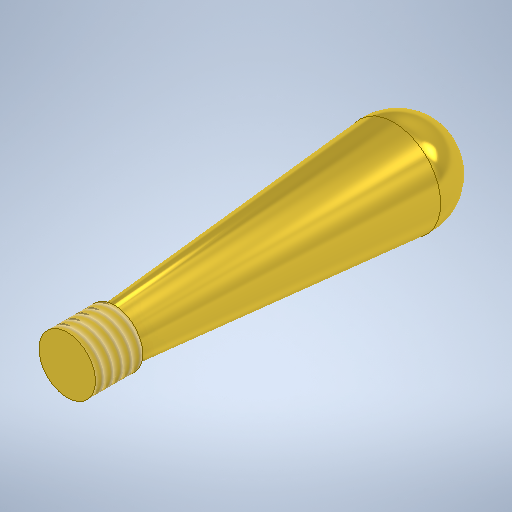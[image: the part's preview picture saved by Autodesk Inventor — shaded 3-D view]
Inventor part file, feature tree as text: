
AUTODESK INVENTOR PART (.ipt)
format: ipt  version: 2025.1 (Build 291241000, 241)  size: 293,888 bytes
history: native  units: mm
features: revolve x1, thread x1, sketch x1
ambient origin geometry x8: Origin, YZ Plane, XZ Plane, XY Plane, X Axis, Y Axis, Z Axis, Center Point
bodies: Solid1 (feature_tree)
feature tree (3):
  revolve  "Revolution1"  [1 undecoded]
  thread  "Thread1"  [1 undecoded]
  sketch  "Sketch1"  dims[d0=3.0mm d3=2.5mm d4=90.0deg d5=20.0mm d6=2.5mm d9=2.5mm d10=10.0mm d11=0.0mm]
note: 2 required parameter values undecoded (feature->parameter linkage not recoverable at this tier; creation-order binding heuristic only, values carry confidence <= 0.55)